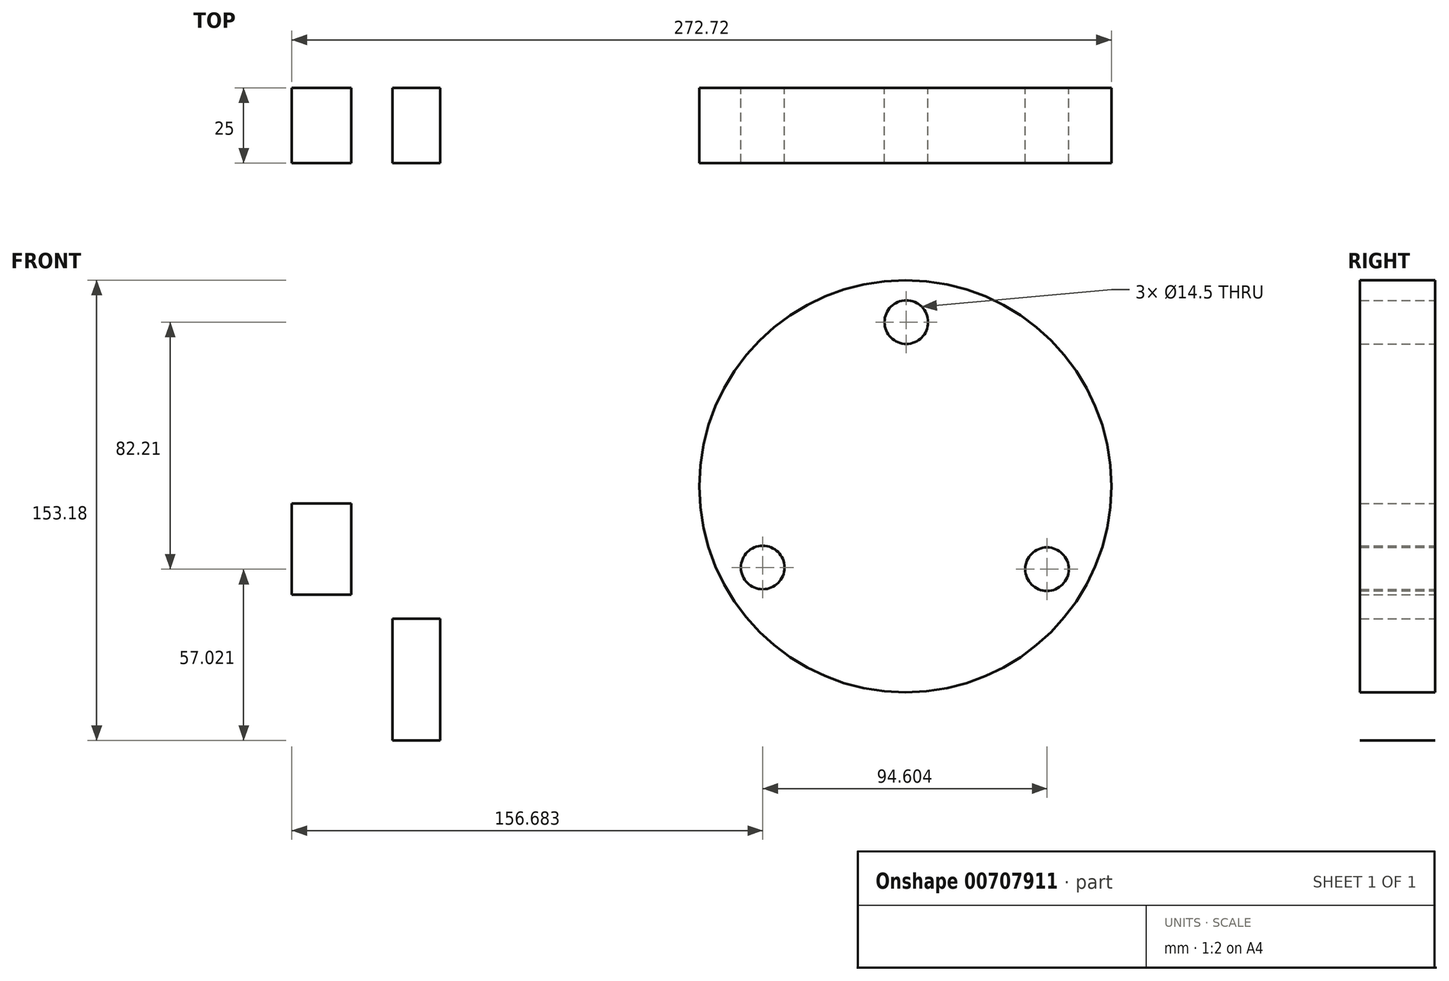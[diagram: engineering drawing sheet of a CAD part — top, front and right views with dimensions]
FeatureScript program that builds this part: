
annotation { "Feature Type Name" : "Feature", "Feature Type Description" : "" }
export const myFeature = defineFeature(function(context is Context, id is Id, definition is map)
    precondition{}
    {
        {
            var Q0;
            Q0=qCreatedBy(makeId("Front.planeOp"),FACE);
            var sketch = newSketch(context, id + "F0", { "sketchPlane" : qUnion([Q0])});
            skLineSegment(sketch, "E0.bottom", {"start": v(-174.45, 49.77) * mm, "end": v(-154.65, 49.77) * mm});
            skLineSegment(sketch, "E0.top", {"start": v(-174.45, 19.46) * mm, "end": v(-154.65, 19.46) * mm});
            skLineSegment(sketch, "E0.left", {"start": v(-174.45, 49.77) * mm, "end": v(-174.45, 19.46) * mm});
            skLineSegment(sketch, "E0.right", {"start": v(-154.65, 49.77) * mm, "end": v(-154.65, 19.46) * mm});
            skLineSegment(sketch, "E1.bottom", {"start": v(-141.02, 11.38) * mm, "end": v(-125.12, 11.38) * mm});
            skLineSegment(sketch, "E1.top", {"start": v(-141.02, -29.14) * mm, "end": v(-125.12, -29.14) * mm});
            skLineSegment(sketch, "E1.left", {"start": v(-141.02, 11.38) * mm, "end": v(-141.02, -29.14) * mm});
            skLineSegment(sketch, "E1.right", {"start": v(-125.12, 11.38) * mm, "end": v(-125.12, -29.14) * mm});
            skSolve(sketch);
        }
        {
            var Q0;
            Q0 = qSketchRegion(id + "F0", true);
            extrude(context, id + "F1", {"entities" : qUnion([Q0]), "depth" : 25 * mm, "offsetDistance" : 25 * mm});
        }
        {
            var Q0;
            Q0=qCreatedBy(makeId("Front.planeOp"),FACE);
            var sketch = newSketch(context, id + "F2", { "sketchPlane" : qUnion([Q0])});
            skCircle(sketch, "E2", {"center": v(29.7, 55.47) * mm, "radius": 68.57 * mm});
            skCircle(sketch, "E3", {"center": v(30.02, 110.1) * mm, "radius": 7.25 * mm});
            skCircle(sketch, "E4.1.0", {"center": v(-17.77, 28.44) * mm, "radius": 7.25 * mm});
            skCircle(sketch, "E4.2.0", {"center": v(76.84, 27.88) * mm, "radius": 7.25 * mm});
            skSolve(sketch);
        }
        {
            var Q0;
            Q0=makeQuery(id+"F2.imprint","IMPRINT",FACE,{"disambiguationData":[TD([[makeQuery(id+"F2.imprint","IMPRINT",EDGE,{"derivedFrom":sQuery(id+"F2.wireOp",EDGE,"E2")}),1.0]])]});
            extrude(context, id + "F3", {"entities" : qUnion([Q0]), "depth" : 25 * mm, "offsetDistance" : 25 * mm});
        }
    });
